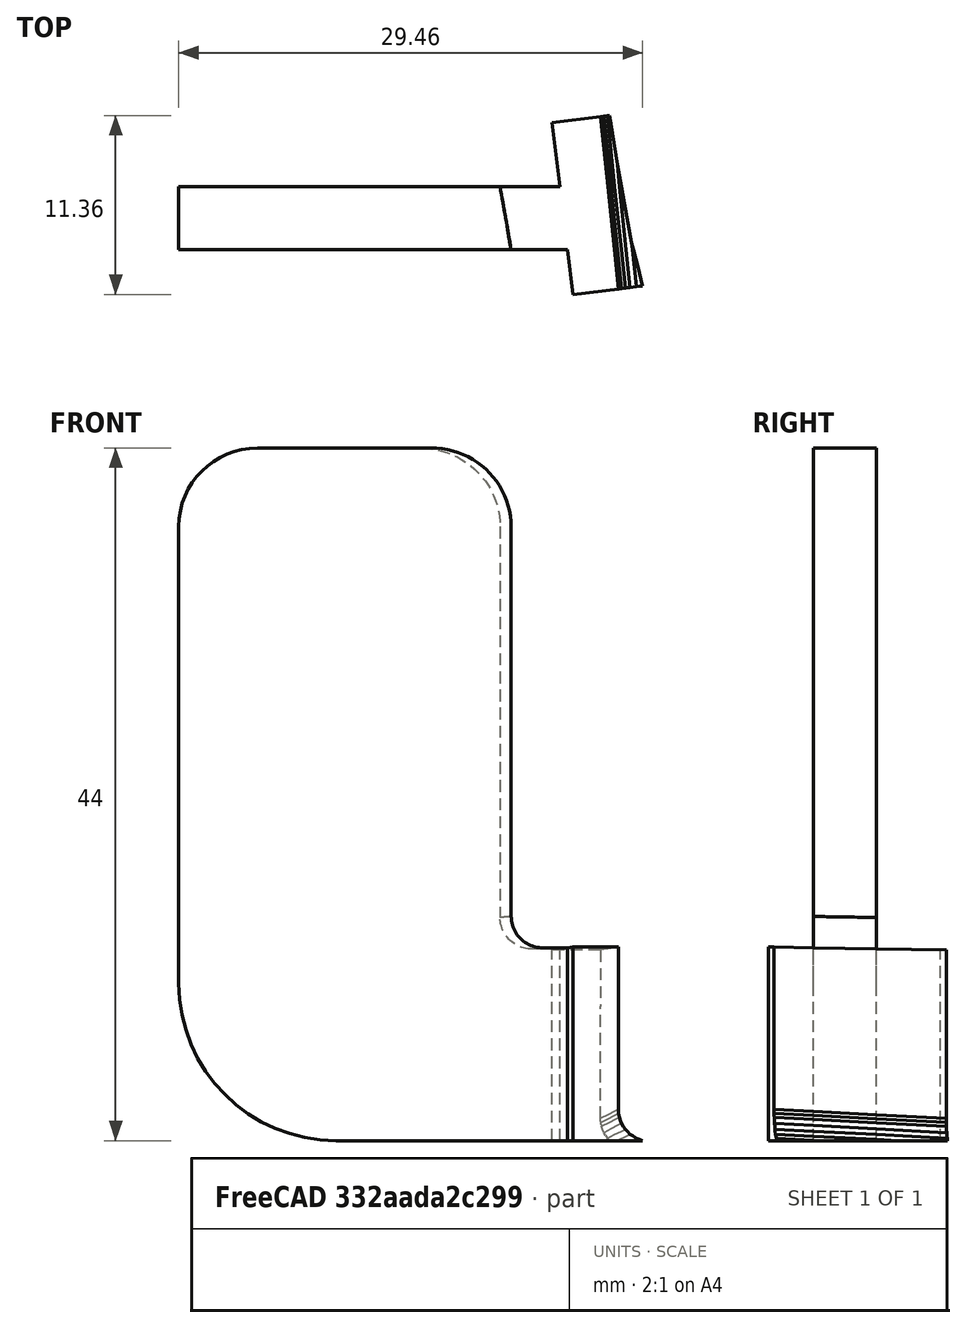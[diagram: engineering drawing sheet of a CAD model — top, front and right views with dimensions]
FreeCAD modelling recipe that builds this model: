
FCSTD DOCUMENT  (FreeCAD 0.16R6704 (Git))
Label: left-bracket
License: All rights reserved
LicenseURL: http://en.wikipedia.org/wiki/All_rights_reserved
objects: Part::Feature×2, Part::Fillet×2, Part::MultiFuse×1, Part::Box×1, Part::Cut×1, Part::Mirroring×1
note: 8 computed .brp shape members not serialized (recipe doc carries the construction recipe); baked Part::Feature solids carry a one-line shape summary decoded from their .brp

FEATURE [Part::Feature] Solid001
  shape: bbox 32.6 x 97.32 x 103 mm, 24 faces (baked)
FEATURE [Part::Feature] Solid003
  shape: bbox 5.752 x 11.37 x 12.3 mm, 22 faces (baked)
FEATURE [Part::MultiFuse] Fusion002
  Shapes = -> [Solid003,Solid001]
FEATURE [Part::Fillet] Fillet009
  Base = -> Fusion002
  Edges = 1 edges r=10: [Edge110]
  Placement = pos=(0,90.5,-451) rot=(0,0,1;0rad)
FEATURE [Part::Box] Box  label="Cube"
  Height = 67
  Length = 28
  Placement = pos=(-13,-6,44) rot=(0,0,1;0rad)
  Width = 13
FEATURE [Part::Cut] Cut
  Base = -> Fillet009
  Tool = -> Box
FEATURE [Part::Fillet] Fillet  label="Right Bracket"
  Base = -> Cut
  Edges = 2 edges r=5: [Edge12,Edge14]
FEATURE [Part::Mirroring] Part__Mirroring  label="Left Bracket"
  Base = (0,0,0)
  Normal = (1,0,0)
  Source = -> Fillet
